# Revit family: Mohlenhof_Внутрипольный конвектор_QSKM CF
name_source: partatom
category: Оборудование
units: mm (PartAtom-declared; Revit-internal decimal feet)

## family parameters
Всегда вертикально = Да
Классификация = Нет
На основе рабочей плоскости = Нет
Общий = Нет
При загрузке вырезать с полостями = Нет
Размер круглого соединителя = Использовать диаметр
Тип детали = Нормальный
Точка расчета площади = Нет

## types (1)
- 195 x 66 CF
    ADSK_Единица измерения = шт.
    ADSK_Завод-изготовитель = Möhlenhoff
    ADSK_Классификация нагрузок = ОВК
    ADSK_Количество = 1
    ADSK_Количество фаз = 1
    ADSK_Коэффициент мощности = 1
    ADSK_Материал = Mohlenhoff_Внутрипольный конвектор
    ADSK_Наименование = Конвектор внутрипольный с тангенциальным вентилятором EC
    ADSK_Напряжение = 230 В
    ADSK_Температура обратной линии = 65 °C
    ADSK_Температура подающей линии = 75 °C
    K = 0.0006
    LT = QSKM
    N = 1.9124
    URL = https://mohlenhoff.pro
    h = 66.5 мм
    Высота = 66 мм
    Диаметр короба = 16 мм
    Диаметр подключения = 10 мм
    Изготовитель = Системные конвекторы Möhlenhoff
    МВ = ♦ : 03. Высокая
    МН = ♦ : 01. Низкая
    МС = ♦ : 02. Средняя
    Материал решетки = Mohlenhoff_Решетка рулонная поперечная
    Обратка_Y = 113 мм
    Обратка_Z = 41 мм
    Отв1_Y = 38 мм
    Отв2_Y = 113 мм
    Отв3_Y = 163 мм
    Отверстие_Диаметр = 30 мм
    Отверстия снизу_Смещение X = 62 мм
    Подача_Y = 38 мм
    Подача_Z = 41 мм
    Смещение вентиляторов = 150 мм
    Сортировка_Позиция = 0
    ТО_Смещение от стенки = 19.25 мм
    ТО_Смещение слева = 245 мм
    ТО_Ширина = 100 мм
    Ширина = 195 мм
